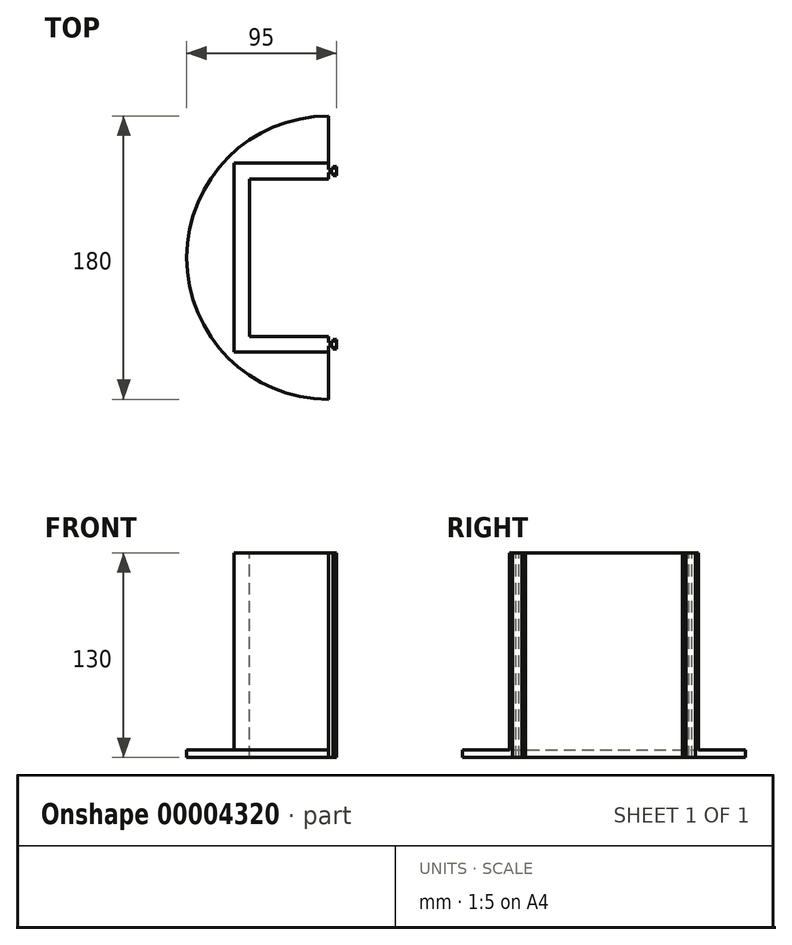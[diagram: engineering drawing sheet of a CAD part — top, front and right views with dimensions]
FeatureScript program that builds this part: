
annotation { "Feature Type Name" : "Feature", "Feature Type Description" : "" }
export const myFeature = defineFeature(function(context is Context, id is Id, definition is map)
    precondition{}
    {
        {
            var Q0;
            Q0=qCreatedBy(makeId("Top.planeOp"),FACE);
            var sketch = newSketch(context, id + "F0", { "sketchPlane" : qUnion([Q0])});
            skArc(sketch, "E0", {"start": v(0, 90) * mm, "mid": v(-90, 0) * mm, "end": v(0, -90) * mm});
            skLineSegment(sketch, "E1", {"start": v(0, -90) * mm, "end": v(0, 90) * mm});
            skLineSegment(sketch, "E2.0", {"start": v(-50, -90) * mm, "end": v(-50, 90) * mm});
            skLineSegment(sketch, "E3", {"start": v(-50, 90) * mm, "end": v(0, 90) * mm});
            skLineSegment(sketch, "E4", {"start": v(-50, -90) * mm, "end": v(0, -90) * mm});
            skLineSegment(sketch, "E5.0", {"start": v(-50, -50) * mm, "end": v(0, -50) * mm});
            skLineSegment(sketch, "E6.0", {"start": v(-50, 50) * mm, "end": v(0, 50) * mm});
            skSolve(sketch);
        }
        {
            var Q0;
            {var subQ0=sQuery(id+"F0.wireOp",EDGE,"E2.0");var subQ1=sQuery(id+"F0.wireOp",EDGE,"E0");var subQ2=makeQuery(id+"F0.imprint","INTERSECT",VERTEX,{"disambiguationData":[OD(0.0)],"derivedFrom":[subQ1,subQ0]});Q0=makeQuery(id+"F0.imprint","IMPRINT",FACE,{"disambiguationData":[TD([[makeQuery(id+"F0.imprint","IMPRINT",EDGE,{"disambiguationData":[TD([[subQ2,-1.0]])],"derivedFrom":subQ1}),1.0]])]});}
            var Q1;
            {var subQ0=sQuery(id+"F0.wireOp",EDGE,"E6.0");Q1=makeQuery(id+"F0.imprint","IMPRINT",FACE,{"disambiguationData":[TD([[makeQuery(id+"F0.imprint","IMPRINT",EDGE,{"derivedFrom":subQ0}),1.0]])]});}
            var Q2;
            {var subQ0=sQuery(id+"F0.wireOp",EDGE,"E5.0");Q2=makeQuery(id+"F0.imprint","IMPRINT",FACE,{"disambiguationData":[TD([[makeQuery(id+"F0.imprint","IMPRINT",EDGE,{"derivedFrom":subQ0}),-1.0]])]});}
            extrude(context, id + "F1", {"entities" : qUnion([Q0, Q1, Q2]), "oppositeDirection" : true, "depth" : 100 * mm});
        }
        {
            var Q0;
            {var subQ0=sQuery(id+"F0.wireOp",EDGE,"E1");Q0=makeQuery(id+"F1.opExtrude","SWEPT_FACE",FACE,{"disambiguationData":[OSD([subQ0]),TDD([makeQuery(id+"F0.imprint","IMPRINT",EDGE,{"disambiguationData":[TD([[makeQuery(id+"F0.imprint","INTERSECT",VERTEX,{"derivedFrom":[subQ0,sQuery(id+"F0.wireOp",EDGE,"E5.0")]}),1.0]])],"derivedFrom":subQ0})])]});}
            var sketch = newSketch(context, id + "F2", { "sketchPlane" : qUnion([Q0])});
            skLineSegment(sketch, "E7.0", {"start": v(-65, -200) * mm, "end": v(-65, 0) * mm});
            skLineSegment(sketch, "E8.0", {"start": v(-75, -200) * mm, "end": v(-75, 0) * mm});
            skLineSegment(sketch, "E9.0", {"start": v(75, -200) * mm, "end": v(75, 0) * mm});
            skLineSegment(sketch, "E10.0", {"start": v(65, -200) * mm, "end": v(65, 0) * mm});
            skLineSegment(sketch, "E11", {"start": v(65, 0) * mm, "end": v(75, 0) * mm});
            skLineSegment(sketch, "E12", {"start": v(65, -200) * mm, "end": v(75, -200) * mm});
            skSolve(sketch);
        }
        {
            var Q0;
            {var subQ0=sQuery(id+"F0.wireOp",EDGE,"E1");var subQ1=makeQuery(id+"F0.imprint","IMPRINT",EDGE,{"disambiguationData":[TD([[makeQuery(id+"F0.imprint","INTERSECT",VERTEX,{"derivedFrom":[subQ0,sQuery(id+"F0.wireOp",EDGE,"E5.0")]}),1.0]])],"derivedFrom":subQ0});var subQ5=sQuery(id+"F2.wireOp",EDGE,"E7.0");var subQ7=makeQuery(id+"F1.opExtrude","CAP_EDGE",EDGE,{"disambiguationData":[OSD([subQ0]),TDD([subQ1])],"isStart":true});var subQ9=makeQuery(id+"F2.imprint","INTERSECT",VERTEX,{"derivedFrom":[subQ7,subQ5]});Q0=makeQuery(id+"F2.imprint","IMPRINT",FACE,{"disambiguationData":[TD([[makeQuery(id+"F2.imprint","IMPRINT",EDGE,{"disambiguationData":[TD([[subQ9,1.0]])],"derivedFrom":subQ5}),1.0]])]});}
            var Q1;
            Q1=makeQuery(id+"F2.imprint","IMPRINT",FACE,{"disambiguationData":[TD([[makeQuery(id+"F2.imprint","IMPRINT",EDGE,{"derivedFrom":sQuery(id+"F2.wireOp",EDGE,"E9.0")}),1.0]])]});
            extrude(context, id + "F3", {"entities" : qUnion([Q0, Q1]), "operationType" : NewBodyOperationType.ADD, "depth" : 10 * mm});
        }
        {
            var Q0;
            Q0=makeQuery(id+"F3.opExtrude","SWEPT_FACE",FACE,{"disambiguationData":[OSD([sQuery(id+"F2.wireOp",EDGE,"E8.0")])]});
            var sketch = newSketch(context, id + "F4", { "sketchPlane" : qUnion([Q0])});
            skLineSegment(sketch, "E13.0", {"start": v(5, -200) * mm, "end": v(5, 0) * mm});
            skSolve(sketch);
        }
        {
            var Q0;
            {var subQ1=sQuery(id+"F2.wireOp",EDGE,"E8.0");var subQ6=makeQuery(id+"F3.opExtrude","CAP_EDGE",EDGE,{"disambiguationData":[OSD([subQ1])],"isStart":false});Q0=makeQuery(id+"F4.imprint","IMPRINT",FACE,{"disambiguationData":[TD([[makeQuery(id+"F4.imprint","IMPRINT",EDGE,{"derivedFrom":subQ6}),1.0]])]});}
            extrude(context, id + "F5", {"entities" : qUnion([Q0]), "operationType" : NewBodyOperationType.ADD, "depth" : 5 * mm});
        }
        {
            var Q0;
            Q0=makeQuery(id+"F3.opExtrude","SWEPT_FACE",FACE,{"disambiguationData":[OSD([sQuery(id+"F2.wireOp",EDGE,"E7.0")])]});
            var sketch = newSketch(context, id + "F6", { "sketchPlane" : qUnion([Q0])});
            skLineSegment(sketch, "E14.0", {"start": v(-5, -200) * mm, "end": v(-5, 0) * mm});
            skSolve(sketch);
        }
        {
            var Q0;
            {var subQ1=sQuery(id+"F2.wireOp",EDGE,"E7.0");var subQ6=makeQuery(id+"F3.opExtrude","CAP_EDGE",EDGE,{"disambiguationData":[OSD([subQ1])],"isStart":false});Q0=makeQuery(id+"F6.imprint","IMPRINT",FACE,{"disambiguationData":[TD([[makeQuery(id+"F6.imprint","IMPRINT",EDGE,{"derivedFrom":subQ6}),-1.0]])]});}
            extrude(context, id + "F7", {"entities" : qUnion([Q0]), "operationType" : NewBodyOperationType.ADD, "depth" : 5 * mm});
        }
        {
            var Q0;
            Q0=makeQuery(id+"F3.opExtrude","SWEPT_FACE",FACE,{"disambiguationData":[OSD([sQuery(id+"F2.wireOp",EDGE,"E10.0")])]});
            var sketch = newSketch(context, id + "F8", { "sketchPlane" : qUnion([Q0])});
            skLineSegment(sketch, "E15.0", {"start": v(5, -200) * mm, "end": v(5, 0) * mm});
            skSolve(sketch);
        }
        {
            var Q0;
            {var subQ2=sQuery(id+"F8.wireOp",EDGE,"E15.0");Q0=makeQuery(id+"F8.imprint","IMPRINT",FACE,{"disambiguationData":[TD([[makeQuery(id+"F8.imprint","IMPRINT",EDGE,{"derivedFrom":subQ2}),-1.0]])]});}
            extrude(context, id + "F9", {"entities" : qUnion([Q0]), "operationType" : NewBodyOperationType.ADD, "depth" : 5 * mm});
        }
        {
            var Q0;
            Q0=makeQuery(id+"F3.opExtrude","SWEPT_FACE",FACE,{"disambiguationData":[OSD([sQuery(id+"F2.wireOp",EDGE,"E9.0")])]});
            var sketch = newSketch(context, id + "F10", { "sketchPlane" : qUnion([Q0])});
            skLineSegment(sketch, "E16.0", {"start": v(-5, -200) * mm, "end": v(-5, 0) * mm});
            skSolve(sketch);
        }
        {
            var Q0;
            {var subQ2=sQuery(id+"F10.wireOp",EDGE,"E16.0");Q0=makeQuery(id+"F10.imprint","IMPRINT",FACE,{"disambiguationData":[TD([[makeQuery(id+"F10.imprint","IMPRINT",EDGE,{"derivedFrom":subQ2}),1.0]])]});}
            extrude(context, id + "F11", {"entities" : qUnion([Q0]), "operationType" : NewBodyOperationType.ADD, "depth" : 5 * mm});
        }
        {
            var Q0;
            {var subQ0=sQuery(id+"F2.wireOp",EDGE,"E12");Q0=makeQuery(id+"F11.boolean.opBoolean","MERGE",FACE,{"derivedFrom":[makeQuery(id+"F9.boolean.opBoolean","MERGE",FACE,{"derivedFrom":[makeQuery(id+"F3.opExtrude","SWEPT_FACE",FACE,{"disambiguationData":[OSD([subQ0])]}),makeQuery(id+"F9.opExtrude","SWEPT_FACE",FACE,{"disambiguationData":[OSD([sQuery(id+"F2.wireOp",EDGE,"E10.0"),subQ0])]})]}),makeQuery(id+"F11.opExtrude","SWEPT_FACE",FACE,{"disambiguationData":[OSD([sQuery(id+"F2.wireOp",EDGE,"E9.0"),subQ0])]})]});}
            extrude(context, id + "F12", {"entities" : qUnion([Q0]), "operationType" : NewBodyOperationType.REMOVE, "oppositeDirection" : true, "depth" : 100 * mm});
        }
        {
            var Q0;
            {var subQ0=sQuery(id+"F0.wireOp",EDGE,"E0");var subQ1=sQuery(id+"F0.wireOp",EDGE,"E1");var subQ2=sQuery(id+"F0.wireOp",EDGE,"E5.0");var subQ3=sQuery(id+"F2.wireOp",EDGE,"E11");var subQ4=makeQuery(id+"F1.opExtrude","CAP_EDGE",EDGE,{"disambiguationData":[OSD([subQ1]),TDD([makeQuery(id+"F0.imprint","IMPRINT",EDGE,{"disambiguationData":[TD([[makeQuery(id+"F0.imprint","INTERSECT",VERTEX,{"derivedFrom":[subQ1,subQ2]}),1.0]])],"derivedFrom":subQ1})])],"isStart":true});var subQ5=sQuery(id+"F2.wireOp",EDGE,"E8.0");var subQ6=makeQuery(id+"F2.imprint","INTERSECT",VERTEX,{"derivedFrom":[subQ4,subQ5]});var subQ7=sQuery(id+"F2.wireOp",EDGE,"E7.0");var subQ8=makeQuery(id+"F2.imprint","INTERSECT",VERTEX,{"derivedFrom":[subQ4,subQ7]});var subQ9=makeQuery(id+"F3.opExtrude","SWEPT_EDGE",EDGE,{"disambiguationData":[OSD([subQ1,subQ5]),TDD([subQ6])]});var subQ10=makeQuery(id+"F3.opExtrude","SWEPT_EDGE",EDGE,{"disambiguationData":[OSD([subQ1,subQ7]),TDD([subQ8])]});Q0=makeQuery(id+"F11.boolean.opBoolean","MERGE",FACE,{"derivedFrom":[makeQuery(id+"F9.boolean.opBoolean","MERGE",FACE,{"derivedFrom":[makeQuery(id+"F7.boolean.opBoolean","MERGE",FACE,{"derivedFrom":[makeQuery(id+"F5.boolean.opBoolean","MERGE",FACE,{"derivedFrom":[makeQuery(id+"F3.boolean.opBoolean","MERGE",FACE,{"derivedFrom":[makeQuery(id+"F1.opExtrude","CAP_FACE",FACE,{"disambiguationData":[OSD([subQ0,subQ1,sQuery(id+"F0.wireOp",EDGE,"E2.0"),subQ2,sQuery(id+"F0.wireOp",EDGE,"E6.0")])],"isStart":true}),makeQuery(id+"F3.opExtrude","SWEPT_FACE",FACE,{"disambiguationData":[OSD([subQ3])]}),makeQuery(id+"F3.opExtrude","SWEPT_FACE",FACE,{"disambiguationData":[OSD([subQ1]),TDD([makeQuery(id+"F2.imprint","IMPRINT",EDGE,{"disambiguationData":[TD([[subQ8,1.0]])],"derivedFrom":subQ4})])]})]}),makeQuery(id+"F5.opExtrude","SWEPT_FACE",FACE,{"disambiguationData":[OSD([subQ1,subQ5]),TDD([makeQuery(id+"F4.imprint","IMPRINT",EDGE,{"disambiguationData":[TD([[makeQuery(id+"F4.imprint","INTERSECT",VERTEX,{"derivedFrom":[subQ9,makeQuery(id+"F3.opExtrude","CAP_EDGE",EDGE,{"disambiguationData":[OSD([subQ5])],"isStart":false})]}),-1.0]])],"derivedFrom":subQ9})])]})]}),makeQuery(id+"F7.opExtrude","SWEPT_FACE",FACE,{"disambiguationData":[OSD([subQ1,subQ7]),TDD([makeQuery(id+"F6.imprint","IMPRINT",EDGE,{"disambiguationData":[TD([[makeQuery(id+"F6.imprint","INTERSECT",VERTEX,{"derivedFrom":[subQ10,makeQuery(id+"F3.opExtrude","CAP_EDGE",EDGE,{"disambiguationData":[OSD([subQ7])],"isStart":false})]}),-1.0]])],"derivedFrom":subQ10})])]})]}),makeQuery(id+"F9.opExtrude","SWEPT_FACE",FACE,{"disambiguationData":[OSD([sQuery(id+"F2.wireOp",EDGE,"E10.0"),subQ3])]})]}),makeQuery(id+"F11.opExtrude","SWEPT_FACE",FACE,{"disambiguationData":[OSD([sQuery(id+"F2.wireOp",EDGE,"E9.0"),subQ3])]})]});}
            extrude(context, id + "F13", {"entities" : qUnion([Q0]), "operationType" : NewBodyOperationType.ADD, "depth" : 10 * mm});
        }
        {
            var Q0;
            Q0=makeQuery(id+"F13.opExtrude","CAP_FACE",FACE,{"disambiguationData":[OSD([sQuery(id+"F0.wireOp",EDGE,"E0"),sQuery(id+"F0.wireOp",EDGE,"E1"),sQuery(id+"F0.wireOp",EDGE,"E2.0"),sQuery(id+"F0.wireOp",EDGE,"E5.0"),sQuery(id+"F0.wireOp",EDGE,"E6.0"),sQuery(id+"F2.wireOp",EDGE,"E7.0"),sQuery(id+"F2.wireOp",EDGE,"E8.0"),sQuery(id+"F2.wireOp",EDGE,"E9.0"),sQuery(id+"F2.wireOp",EDGE,"E10.0"),sQuery(id+"F2.wireOp",EDGE,"E11")])],"isStart":false});
            extrude(context, id + "F14", {"entities" : qUnion([Q0]), "operationType" : NewBodyOperationType.ADD, "depth" : 20 * mm});
        }
        {
            var Q0;
            Q0=makeQuery(id+"F14.opExtrude","CAP_FACE",FACE,{"disambiguationData":[OSD([sQuery(id+"F0.wireOp",EDGE,"E0"),sQuery(id+"F0.wireOp",EDGE,"E1"),sQuery(id+"F0.wireOp",EDGE,"E2.0"),sQuery(id+"F0.wireOp",EDGE,"E5.0"),sQuery(id+"F0.wireOp",EDGE,"E6.0"),sQuery(id+"F2.wireOp",EDGE,"E7.0"),sQuery(id+"F2.wireOp",EDGE,"E8.0"),sQuery(id+"F2.wireOp",EDGE,"E9.0"),sQuery(id+"F2.wireOp",EDGE,"E10.0"),sQuery(id+"F2.wireOp",EDGE,"E11")])],"isStart":false});
            var sketch = newSketch(context, id + "F15", { "sketchPlane" : qUnion([Q0])});
            skLineSegment(sketch, "E17.0", {"start": v(-60, -60) * mm, "end": v(0, -60) * mm});
            skLineSegment(sketch, "E18.0", {"start": v(-60, -60) * mm, "end": v(-60, 60) * mm});
            skLineSegment(sketch, "E19.0", {"start": v(-60, 60) * mm, "end": v(0, 60) * mm});
            skSolve(sketch);
        }
        {
            var Q0;
            {var subQ23=sQuery(id+"F15.wireOp",EDGE,"E17.0");Q0=makeQuery(id+"F15.imprint","IMPRINT",FACE,{"disambiguationData":[TD([[makeQuery(id+"F15.imprint","IMPRINT",EDGE,{"derivedFrom":subQ23}),-1.0]])]});}
            extrude(context, id + "F16", {"entities" : qUnion([Q0]), "operationType" : NewBodyOperationType.REMOVE, "oppositeDirection" : true, "depth" : 130 * mm});
        }
        {
            var Q0;
            {var subQ0=sQuery(id+"F0.wireOp",EDGE,"E1");var subQ1=sQuery(id+"F0.wireOp",EDGE,"E5.0");var subQ3=makeQuery(id+"F0.imprint","IMPRINT",EDGE,{"disambiguationData":[TD([[makeQuery(id+"F0.imprint","INTERSECT",VERTEX,{"derivedFrom":[subQ0,subQ1]}),1.0]])],"derivedFrom":subQ0});var subQ4=makeQuery(id+"F1.opExtrude","SWEPT_FACE",FACE,{"disambiguationData":[OSD([subQ0]),TDD([subQ3])]});var subQ10=makeQuery(id+"F1.opExtrude","CAP_EDGE",EDGE,{"disambiguationData":[OSD([subQ0]),TDD([subQ3])],"isStart":true});var subQ12=makeQuery(id+"F1.opExtrude","SWEPT_FACE",FACE,{"disambiguationData":[OSD([subQ1])]});var subQ16=makeQuery(id+"F3.boolean.opBoolean","SPLIT",EDGE,{"disambiguationData":[TD([subQ12])],"derivedFrom":subQ10});Q0=makeQuery(id+"F14.boolean.opBoolean","MERGE",FACE,{"derivedFrom":[makeQuery(id+"F13.boolean.opBoolean","MERGE",FACE,{"derivedFrom":[makeQuery(id+"F3.boolean.opBoolean","SPLIT",FACE,{"disambiguationData":[TD([subQ12])],"derivedFrom":subQ4}),makeQuery(id+"F13.opExtrude","SWEPT_FACE",FACE,{"disambiguationData":[OSD([subQ0]),TDD([subQ16])]})]}),makeQuery(id+"F14.opExtrude","SWEPT_FACE",FACE,{"disambiguationData":[OSD([subQ0]),TDD([makeQuery(id+"F13.opExtrude","CAP_EDGE",EDGE,{"disambiguationData":[OSD([subQ0]),TDD([subQ16])],"isStart":false})])]})]});}
            var sketch = newSketch(context, id + "F17", { "sketchPlane" : qUnion([Q0])});
            skLineSegment(sketch, "E20.0", {"start": v(-54, -100) * mm, "end": v(-54, 30) * mm});
            skLineSegment(sketch, "E21.0", {"start": v(-56, -100) * mm, "end": v(-56, 30) * mm});
            skLineSegment(sketch, "E22", {"start": v(-54, -100) * mm, "end": v(-56, -100) * mm});
            skLineSegment(sketch, "E23", {"start": v(-56, 30) * mm, "end": v(-54, 30) * mm});
            skLineSegment(sketch, "E24", {"start": v(-56, -100) * mm, "end": v(-54, -100) * mm});
            skLineSegment(sketch, "E25.0", {"start": v(56, -100) * mm, "end": v(56, 30) * mm});
            skLineSegment(sketch, "E26.0", {"start": v(54, -100) * mm, "end": v(54, 30) * mm});
            skLineSegment(sketch, "E27", {"start": v(56, -100) * mm, "end": v(54, -100) * mm});
            skLineSegment(sketch, "E28", {"start": v(54, 30) * mm, "end": v(56, 30) * mm});
            skSolve(sketch);
        }
        {
            var Q0;
            Q0=makeQuery(id+"F17.imprint","IMPRINT",FACE,{"disambiguationData":[TD([[makeQuery(id+"F17.imprint","IMPRINT",EDGE,{"derivedFrom":sQuery(id+"F17.wireOp",EDGE,"E25.0")}),1.0]])]});
            var Q1;
            Q1=makeQuery(id+"F17.imprint","IMPRINT",FACE,{"disambiguationData":[TD([[makeQuery(id+"F17.imprint","IMPRINT",EDGE,{"derivedFrom":sQuery(id+"F17.wireOp",EDGE,"E20.0")}),1.0]])]});
            extrude(context, id + "F18", {"entities" : qUnion([Q0, Q1]), "operationType" : NewBodyOperationType.ADD, "depth" : 5 * mm});
        }
        {
            var Q0;
            Q0=makeQuery(id+"F18.opExtrude","SWEPT_FACE",FACE,{"disambiguationData":[OSD([sQuery(id+"F17.wireOp",EDGE,"E21.0")])]});
            var sketch = newSketch(context, id + "F19", { "sketchPlane" : qUnion([Q0])});
            skLineSegment(sketch, "E29.0", {"start": v(3, -100) * mm, "end": v(3, 30) * mm});
            skSolve(sketch);
        }
        {
            var Q0;
            Q0=makeQuery(id+"F18.opExtrude","SWEPT_FACE",FACE,{"disambiguationData":[OSD([sQuery(id+"F17.wireOp",EDGE,"E20.0")])]});
            var sketch = newSketch(context, id + "F20", { "sketchPlane" : qUnion([Q0])});
            skLineSegment(sketch, "E30.0", {"start": v(-3, -100) * mm, "end": v(-3, 30) * mm});
            skSolve(sketch);
        }
        {
            var Q0;
            Q0=makeQuery(id+"F18.opExtrude","SWEPT_FACE",FACE,{"disambiguationData":[OSD([sQuery(id+"F17.wireOp",EDGE,"E26.0")])]});
            var sketch = newSketch(context, id + "F21", { "sketchPlane" : qUnion([Q0])});
            skLineSegment(sketch, "E31.0", {"start": v(3, -100) * mm, "end": v(3, 30) * mm});
            skSolve(sketch);
        }
        {
            var Q0;
            Q0=makeQuery(id+"F18.opExtrude","SWEPT_FACE",FACE,{"disambiguationData":[OSD([sQuery(id+"F17.wireOp",EDGE,"E25.0")])]});
            var sketch = newSketch(context, id + "F22", { "sketchPlane" : qUnion([Q0])});
            skLineSegment(sketch, "E32.0", {"start": v(-3, -100) * mm, "end": v(-3, 30) * mm});
            skSolve(sketch);
        }
        {
            var Q0;
            {var subQ3=sQuery(id+"F19.wireOp",EDGE,"E29.0");Q0=makeQuery(id+"F19.imprint","IMPRINT",FACE,{"disambiguationData":[TD([[makeQuery(id+"F19.imprint","IMPRINT",EDGE,{"derivedFrom":subQ3}),-1.0]])]});}
            extrude(context, id + "F23", {"entities" : qUnion([Q0]), "operationType" : NewBodyOperationType.ADD, "depth" : 2 * mm});
        }
        {
            var Q0;
            {var subQ3=sQuery(id+"F20.wireOp",EDGE,"E30.0");Q0=makeQuery(id+"F20.imprint","IMPRINT",FACE,{"disambiguationData":[TD([[makeQuery(id+"F20.imprint","IMPRINT",EDGE,{"derivedFrom":subQ3}),1.0]])]});}
            extrude(context, id + "F24", {"entities" : qUnion([Q0]), "operationType" : NewBodyOperationType.ADD, "depth" : 2 * mm});
        }
        {
            var Q0;
            {var subQ2=sQuery(id+"F21.wireOp",EDGE,"E31.0");Q0=makeQuery(id+"F21.imprint","IMPRINT",FACE,{"disambiguationData":[TD([[makeQuery(id+"F21.imprint","IMPRINT",EDGE,{"derivedFrom":subQ2}),-1.0]])]});}
            extrude(context, id + "F25", {"entities" : qUnion([Q0]), "operationType" : NewBodyOperationType.ADD, "depth" : 2 * mm});
        }
        {
            var Q0;
            {var subQ2=sQuery(id+"F22.wireOp",EDGE,"E32.0");Q0=makeQuery(id+"F22.imprint","IMPRINT",FACE,{"disambiguationData":[TD([[makeQuery(id+"F22.imprint","IMPRINT",EDGE,{"derivedFrom":subQ2}),1.0]])]});}
            extrude(context, id + "F26", {"entities" : qUnion([Q0]), "operationType" : NewBodyOperationType.ADD, "depth" : 2 * mm});
        }
        {
            var Q0;
            {var subQ0=sQuery(id+"F0.wireOp",EDGE,"E0");var subQ1=sQuery(id+"F0.wireOp",EDGE,"E1");var subQ2=sQuery(id+"F0.wireOp",EDGE,"E5.0");var subQ3=makeQuery(id+"F1.opExtrude","CAP_EDGE",EDGE,{"disambiguationData":[OSD([subQ1]),TDD([makeQuery(id+"F0.imprint","IMPRINT",EDGE,{"disambiguationData":[TD([[makeQuery(id+"F0.imprint","INTERSECT",VERTEX,{"derivedFrom":[subQ1,subQ2]}),1.0]])],"derivedFrom":subQ1})])],"isStart":false});var subQ4=sQuery(id+"F2.wireOp",EDGE,"E8.0");var subQ5=makeQuery(id+"F2.imprint","INTERSECT",VERTEX,{"derivedFrom":[subQ3,subQ4]});var subQ6=sQuery(id+"F2.wireOp",EDGE,"E7.0");var subQ7=makeQuery(id+"F2.imprint","INTERSECT",VERTEX,{"derivedFrom":[subQ3,subQ6]});var subQ8=makeQuery(id+"F3.opExtrude","SWEPT_EDGE",EDGE,{"disambiguationData":[OSD([subQ1,subQ4]),TDD([subQ5])]});var subQ9=makeQuery(id+"F3.opExtrude","SWEPT_EDGE",EDGE,{"disambiguationData":[OSD([subQ1,subQ6]),TDD([subQ7])]});var subQ10=sQuery(id+"F17.wireOp",EDGE,"E24");var subQ11=sQuery(id+"F17.wireOp",EDGE,"E27");Q0=makeQuery(id+"F26.boolean.opBoolean","MERGE",FACE,{"derivedFrom":[makeQuery(id+"F25.boolean.opBoolean","MERGE",FACE,{"derivedFrom":[makeQuery(id+"F24.boolean.opBoolean","MERGE",FACE,{"derivedFrom":[makeQuery(id+"F23.boolean.opBoolean","MERGE",FACE,{"derivedFrom":[makeQuery(id+"F18.boolean.opBoolean","MERGE",FACE,{"derivedFrom":[makeQuery(id+"F12.boolean.opBoolean","MERGE",FACE,{"derivedFrom":[makeQuery(id+"F7.boolean.opBoolean","MERGE",FACE,{"derivedFrom":[makeQuery(id+"F5.boolean.opBoolean","MERGE",FACE,{"derivedFrom":[makeQuery(id+"F3.boolean.opBoolean","MERGE",FACE,{"derivedFrom":[makeQuery(id+"F1.opExtrude","CAP_FACE",FACE,{"disambiguationData":[OSD([subQ0,subQ1,sQuery(id+"F0.wireOp",EDGE,"E2.0"),subQ2,sQuery(id+"F0.wireOp",EDGE,"E6.0")])],"isStart":false}),makeQuery(id+"F3.opExtrude","SWEPT_FACE",FACE,{"disambiguationData":[OSD([subQ1]),TDD([makeQuery(id+"F2.imprint","IMPRINT",EDGE,{"disambiguationData":[TD([[subQ7,1.0]])],"derivedFrom":subQ3})])]})]}),makeQuery(id+"F5.opExtrude","SWEPT_FACE",FACE,{"disambiguationData":[OSD([subQ1,subQ4]),TDD([makeQuery(id+"F4.imprint","IMPRINT",EDGE,{"disambiguationData":[TD([[makeQuery(id+"F4.imprint","INTERSECT",VERTEX,{"derivedFrom":[subQ8,makeQuery(id+"F3.opExtrude","CAP_EDGE",EDGE,{"disambiguationData":[OSD([subQ4])],"isStart":false})]}),-1.0]])],"derivedFrom":subQ8})])]})]}),makeQuery(id+"F7.opExtrude","SWEPT_FACE",FACE,{"disambiguationData":[OSD([subQ1,subQ6]),TDD([makeQuery(id+"F6.imprint","IMPRINT",EDGE,{"disambiguationData":[TD([[makeQuery(id+"F6.imprint","INTERSECT",VERTEX,{"derivedFrom":[subQ9,makeQuery(id+"F3.opExtrude","CAP_EDGE",EDGE,{"disambiguationData":[OSD([subQ6])],"isStart":false})]}),-1.0]])],"derivedFrom":subQ9})])]})]}),makeQuery(id+"F12.opExtrude","CAP_FACE",FACE,{"disambiguationData":[OSD([sQuery(id+"F2.wireOp",EDGE,"E9.0"),sQuery(id+"F2.wireOp",EDGE,"E10.0"),sQuery(id+"F2.wireOp",EDGE,"E12")])],"isStart":false})]}),makeQuery(id+"F18.opExtrude","SWEPT_FACE",FACE,{"disambiguationData":[OSD([subQ10])]}),makeQuery(id+"F18.opExtrude","SWEPT_FACE",FACE,{"disambiguationData":[OSD([subQ11])]})]}),makeQuery(id+"F23.opExtrude","SWEPT_FACE",FACE,{"disambiguationData":[OSD([subQ1,sQuery(id+"F17.wireOp",EDGE,"E21.0"),subQ10])]})]}),makeQuery(id+"F24.opExtrude","SWEPT_FACE",FACE,{"disambiguationData":[OSD([subQ1,sQuery(id+"F17.wireOp",EDGE,"E20.0"),subQ10])]})]}),makeQuery(id+"F25.opExtrude","SWEPT_FACE",FACE,{"disambiguationData":[OSD([sQuery(id+"F17.wireOp",EDGE,"E26.0"),subQ11])]})]}),makeQuery(id+"F26.opExtrude","SWEPT_FACE",FACE,{"disambiguationData":[OSD([sQuery(id+"F17.wireOp",EDGE,"E25.0"),subQ11])]})]});}
            var sketch = newSketch(context, id + "F27", { "sketchPlane" : qUnion([Q0])});
            skArc(sketch, "E33", {"start": v(0, 90) * mm, "mid": v(-90, 0) * mm, "end": v(0, -90) * mm});
            skLineSegment(sketch, "E34", {"start": v(0, -60) * mm, "end": v(0, -90) * mm});
            skLineSegment(sketch, "E35", {"start": v(0, 60) * mm, "end": v(0, 90) * mm});
            skSolve(sketch);
        }
        {
            var Q0;
            Q0=makeQuery(id+"F27.imprint","IMPRINT",FACE,{"disambiguationData":[TD([[makeQuery(id+"F27.imprint","IMPRINT",EDGE,{"derivedFrom":sQuery(id+"F27.wireOp",EDGE,"E33")}),1.0]])]});
            extrude(context, id + "F28", {"entities" : qUnion([Q0]), "operationType" : NewBodyOperationType.ADD, "oppositeDirection" : true, "depth" : 5 * mm});
        }
    });
